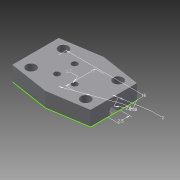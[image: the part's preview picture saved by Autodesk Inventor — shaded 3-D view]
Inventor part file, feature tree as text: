
AUTODESK INVENTOR PART (.ipt)
format: ipt  version: 2013 SP2 (Build 170200200, 200)  size: 119,808 bytes
history: native  units: mm
features: sketch x3, extrude x1, sweep x1
ambient origin geometry x8: Origin, YZ Plane, XZ Plane, XY Plane, X Axis, Y Axis, Z Axis, Center Point
feature tree (5):
  extrude  "Extrusion2"  Depth=1.7mm
  sweep  "Sweep1"
  sketch  "Sketch1"  dims[d1=2.5mm d2=2.0mm d3=6.0mm d4=16.0mm d5=2.8mm d8=3.0mm d9=0.0mm d11=1.7mm]
  sketch  "Sketch2"  dims[d12=0.0mm d13=5.08mm d14=1.2mm]
  sketch  "Sketch3"  dims[d19=0.7mm]
